# Revit family: FP-Revit18-OB60SD13PLX1-Oven-0-AU-IE-NZ-UK-90002665A
name_source: partatom
category: Specialty Equipment
revit_build: Autodesk Revit 2018 (Build: 20170223_1515(x64)
units: mm (PartAtom-declared; Revit-internal decimal feet)

## family parameters
Always vertical = Yes
Cut with Voids When Loaded = Yes
OmniClass Number = 23.40.40.14.17.11
OmniClass Title = Cookers, Ovens, Stoves
Part Type = Normal
Room Calculation Point = No
Round Connector Dimension = Use Diameter
Shared = No
Work Plane-Based = No

## types (1)
- OB60SD13PLX1
    Cavity - Depth = 550 mm
    Cavity - Height = 580 mm  [stored 1.90289 ft]
    Cavity - Width = 560 mm  [stored 1.83727 ft]
    Chassis - Depth = 545 mm  [stored 1.78806 ft]
    Chassis - Height = 575 mm
    Chassis - Width = 556 mm  [stored 1.82415 ft]
    Connector Note - Electrical = 220-240 V, 12.8 - 13.8 A, 50 Hz
    Description = 60cm Built-In Oven
    Manufacturer = Fisher & Paykel Appliances
    Material - Bezel = Fisher & Paykel - Bezel Red
    Material - Body = Fisher & Paykel - Grey
    Material - Buttons and Dials = Fisher & Paykel - Stainless Steel
    Material - Glass = Fisher & Paykel - Glass, Black
    Material - Handle = Fisher & Paykel - Aluminium
    Material - Logo = Fisher & Paykel - Graphics Grey
    Material - Structure = Fisher & Paykel - Black
    Material - Trim = Fisher & Paykel - Stainless Steel
    Model = OB60SD13PLX1
    Product - Depth = 565 mm  [stored 1.85367 ft]
    Product - Height = 598 mm  [stored 1.96194 ft]
    Product - Width = 596 mm  [stored 1.95538 ft]
    URL = www.fisherpaykel.com
    Visibility - Clearance Required = Yes

note: [stored X ft] marks values corroborated as IEEE doubles in the binary element streams (Revit-internal decimal feet)

## geometry (parser evidence)
native form markers: Sweep x2
no freeform markers — native parametric forms only
